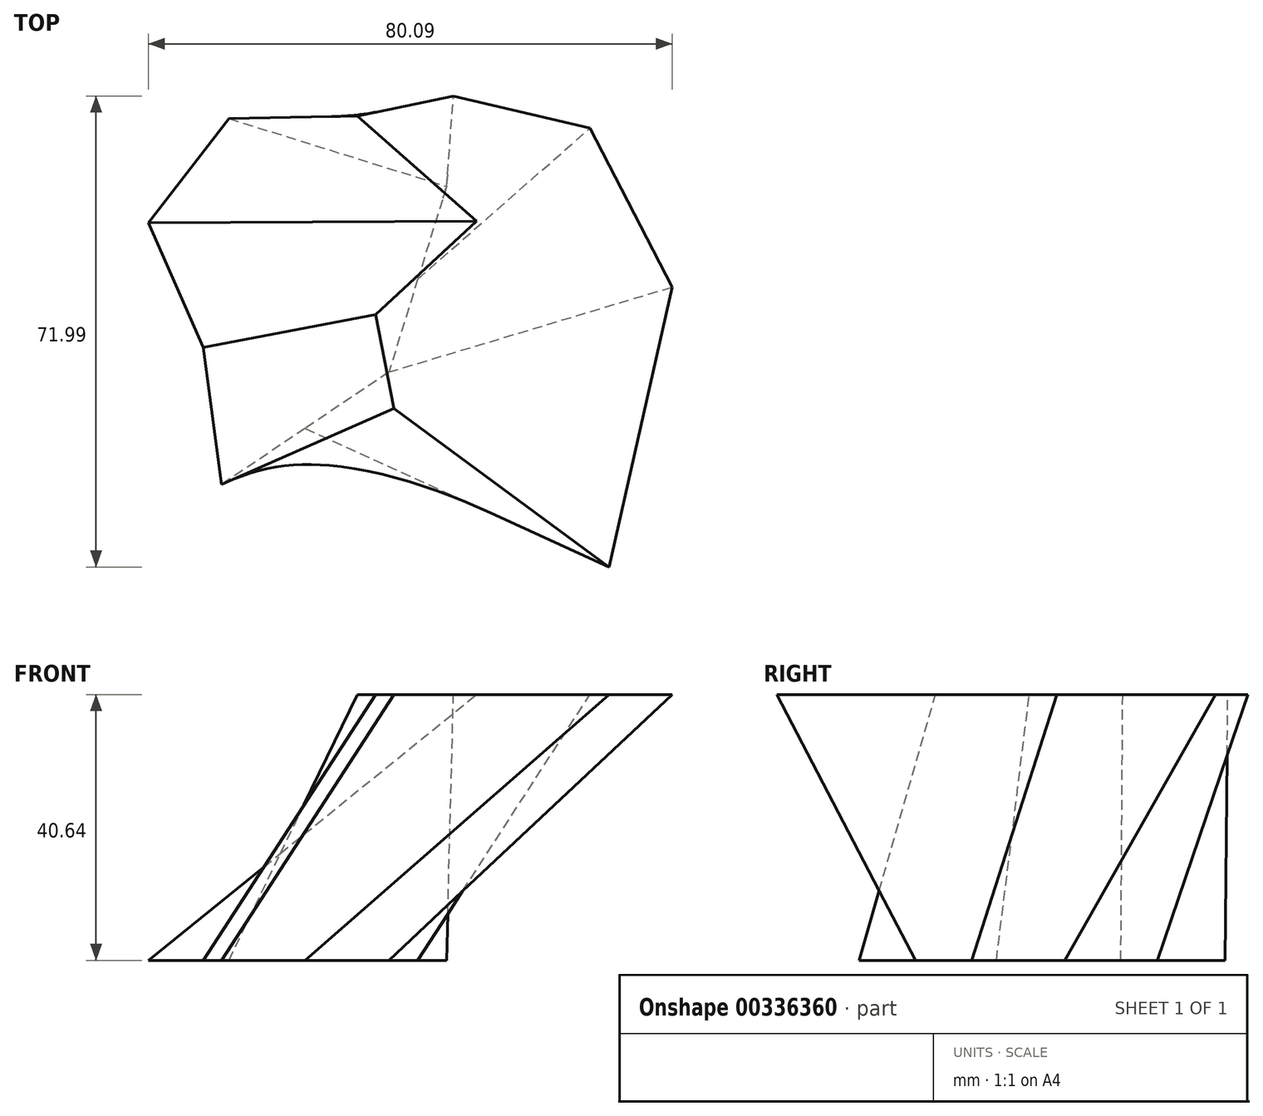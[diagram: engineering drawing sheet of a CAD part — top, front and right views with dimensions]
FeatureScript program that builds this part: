
annotation { "Feature Type Name" : "Feature", "Feature Type Description" : "" }
export const myFeature = defineFeature(function(context is Context, id is Id, definition is map)
    precondition{}
    {
        {
            var Q0;
            Q0=qCreatedBy(makeId("Top.planeOp"),FACE);
            var sketch = newSketch(context, id + "F0", { "sketchPlane" : qUnion([Q0])});
            skLineSegment(sketch, "E0", {"start": v(-8.67, 29.93) * mm, "end": v(24.62, 19.58) * mm});
            skLineSegment(sketch, "E1", {"start": v(24.62, 19.58) * mm, "end": v(15.79, -8.82) * mm});
            skLineSegment(sketch, "E2", {"start": v(15.79, -8.82) * mm, "end": v(-9.8, -26.02) * mm});
            skLineSegment(sketch, "E3", {"start": v(-9.8, -26.02) * mm, "end": v(-12.59, -5.04) * mm});
            skLineSegment(sketch, "E4", {"start": v(-12.59, -5.04) * mm, "end": v(-20.98, 13.99) * mm});
            skLineSegment(sketch, "E5", {"start": v(-20.98, 13.99) * mm, "end": v(-8.67, 29.93) * mm});
            skSolve(sketch);
        }
        {
            var Q0;
            Q0=qCreatedBy(makeId("Top.planeOp"),FACE);
            cPlane(context, id + "F1", {"entities" : qUnion([Q0]), "cplaneType" : CPlaneType.OFFSET, "offset" : 40.64 * mm, "width" : 152.4 * mm, "height" : 152.4 * mm});
        }
        {
            var Q0;
            Q0=qCreatedBy(id+"F1.planeOp",FACE);
            var sketch = newSketch(context, id + "F2", { "sketchPlane" : qUnion([Q0])});
            skLineSegment(sketch, "E6", {"start": v(29.22, 14.28) * mm, "end": v(10.96, 30.33) * mm});
            skLineSegment(sketch, "E7", {"start": v(10.96, 30.33) * mm, "end": v(25.66, 33.4) * mm});
            skLineSegment(sketch, "E8", {"start": v(25.66, 33.4) * mm, "end": v(46.54, 28.48) * mm});
            skLineSegment(sketch, "E9", {"start": v(46.54, 28.48) * mm, "end": v(59.1, 4.19) * mm});
            skLineSegment(sketch, "E10", {"start": v(59.1, 4.19) * mm, "end": v(49.47, -38.6) * mm});
            skLineSegment(sketch, "E11", {"start": v(49.47, -38.6) * mm, "end": v(16.59, -14.34) * mm});
            skLineSegment(sketch, "E12", {"start": v(16.59, -14.34) * mm, "end": v(13.74, 0) * mm});
            skLineSegment(sketch, "E13", {"start": v(13.74, 0) * mm, "end": v(29.22, 14.28) * mm});
            skSolve(sketch);
        }
        {
            var Q0;
            Q0=makeQuery(id+"F0.imprint","IMPRINT",FACE,{"disambiguationData":[TD([[makeQuery(id+"F0.imprint","IMPRINT",EDGE,{"derivedFrom":sQuery(id+"F0.wireOp",EDGE,"E0")}),-1.0]])]});
            var Q1;
            Q1=makeQuery(id+"F2.imprint","IMPRINT",FACE,{"disambiguationData":[TD([[makeQuery(id+"F2.imprint","IMPRINT",EDGE,{"derivedFrom":sQuery(id+"F2.wireOp",EDGE,"E6")}),-1.0]])]});
            loft(context, id + "F3", {"sheetProfilesArray" : [{ "sheetProfileEntities" : qUnion([Q0]) }, { "sheetProfileEntities" : qUnion([Q1]) }]});
        }
    });
